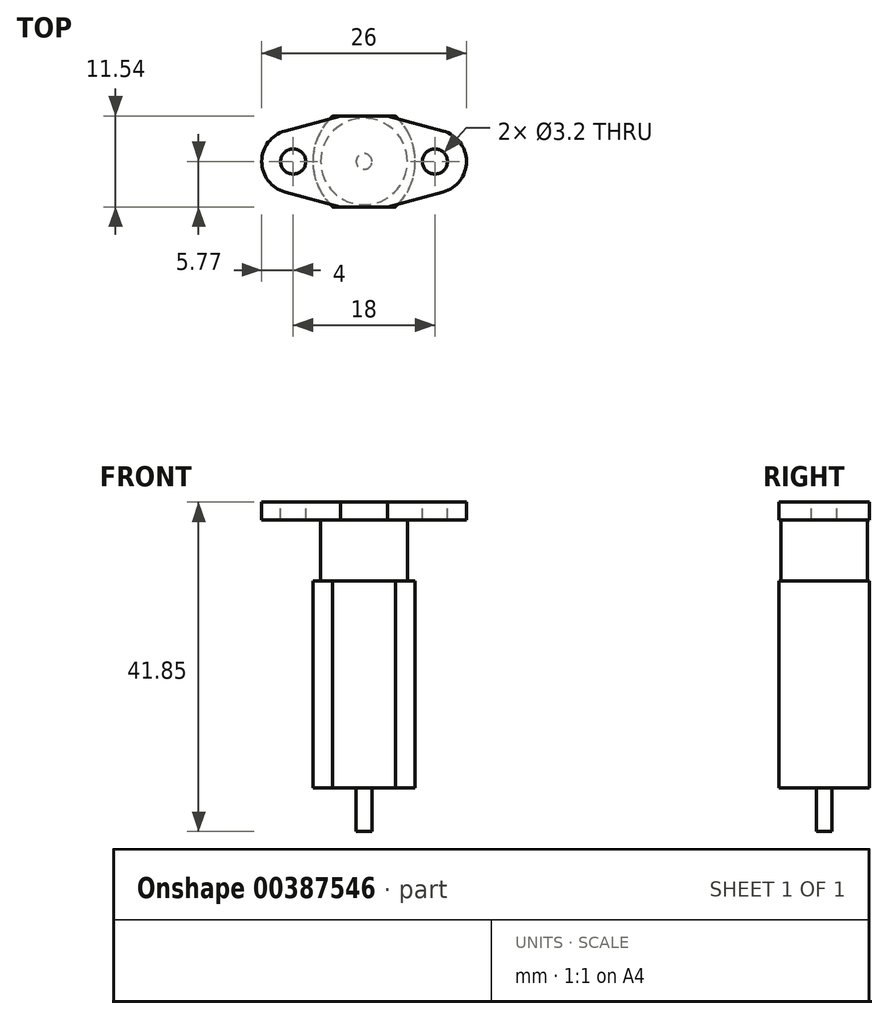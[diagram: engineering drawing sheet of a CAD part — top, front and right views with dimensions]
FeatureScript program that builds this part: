
annotation { "Feature Type Name" : "Feature", "Feature Type Description" : "" }
export const myFeature = defineFeature(function(context is Context, id is Id, definition is map)
    precondition{}
    {
        {
            var Q0;
            Q0=qCreatedBy(makeId("Top.planeOp"),FACE);
            var sketch = newSketch(context, id + "F0", { "sketchPlane" : qUnion([Q0])});
            skLineSegment(sketch, "E0", {"start": v(-3, 5.77) * mm, "end": v(3, 5.77) * mm});
            skLineSegment(sketch, "E1", {"start": v(3, 5.76) * mm, "end": v(10.04, 3.86) * mm});
            skLineSegment(sketch, "E2", {"start": v(10.04, -3.86) * mm, "end": v(3, -5.77) * mm});
            skLineSegment(sketch, "E3", {"start": v(3, -5.77) * mm, "end": v(-3, -5.77) * mm});
            skLineSegment(sketch, "E4", {"start": v(-3, -5.77) * mm, "end": v(-10.04, -3.86) * mm});
            skLineSegment(sketch, "E5", {"start": v(-10.04, 3.86) * mm, "end": v(-3, 5.77) * mm});
            skPoint(sketch, "E6.visualSharp", {"position": v(-24.33, 0) * mm});
            skArc(sketch, "E6.filletArc", {"start": v(-10.04, 3.86) * mm, "mid": v(-13, 0) * mm, "end": v(-10.04, -3.86) * mm});
            skPoint(sketch, "E7.visualSharp", {"position": v(24.33, 0) * mm});
            skArc(sketch, "E7.filletArc", {"start": v(10.04, -3.86) * mm, "mid": v(13, 0) * mm, "end": v(10.04, 3.86) * mm});
            skLineSegment(sketch, "E8", {"start": v(0, -5.77) * mm, "end": v(0, 5.77) * mm, "construction": true});
            skLineSegment(sketch, "E9", {"start": v(-9, 0) * mm, "end": v(9, 0) * mm, "construction": true});
            skCircle(sketch, "E10", {"center": v(-9, 0) * mm, "radius": 1.6 * mm});
            skCircle(sketch, "E11", {"center": v(9, 0) * mm, "radius": 1.6 * mm});
            skSolve(sketch);
        }
        {
            var Q0;
            Q0=qSketchRegion(id+"F0",true);
            extrude(context, id + "F1", {"entities" : qUnion([Q0]), "oppositeDirection" : true, "depth" : 2.3 * mm});
        }
        {
            var Q0;
            Q0=makeQuery(id+"F1.opExtrude","CAP_FACE",FACE,{"disambiguationData":[OSD([sQuery(id+"F0.wireOp",EDGE,"E0"),sQuery(id+"F0.wireOp",EDGE,"E1"),sQuery(id+"F0.wireOp",EDGE,"E2"),sQuery(id+"F0.wireOp",EDGE,"E3"),sQuery(id+"F0.wireOp",EDGE,"E4"),sQuery(id+"F0.wireOp",EDGE,"E5"),sQuery(id+"F0.wireOp",EDGE,"E6.filletArc"),sQuery(id+"F0.wireOp",EDGE,"E7.filletArc"),sQuery(id+"F0.wireOp",EDGE,"E10"),sQuery(id+"F0.wireOp",EDGE,"E11")])],"isStart":false});
            var sketch = newSketch(context, id + "F2", { "sketchPlane" : qUnion([Q0])});
            skCircle(sketch, "E12", {"center": v(0, 0) * mm, "radius": 5.5 * mm});
            skPoint(sketch, "E12.centerSnap0", {"position": v(-13, 0) * mm});
            skPoint(sketch, "E12.centerSnap1", {"position": v(0, 5.77) * mm});
            skSolve(sketch);
        }
        {
            var Q0;
            Q0=qSketchRegion(id+"F2",true);
            extrude(context, id + "F3", {"entities" : qUnion([Q0]), "operationType" : NewBodyOperationType.ADD, "depth" : 7.7 * mm});
        }
        {
            var Q0;
            Q0=makeQuery(id+"F3.opExtrude","CAP_FACE",FACE,{"disambiguationData":[OSD([sQuery(id+"F2.wireOp",EDGE,"E12")])],"isStart":false});
            var sketch = newSketch(context, id + "F4", { "sketchPlane" : qUnion([Q0])});
            skLineSegment(sketch, "E13", {"start": v(-4, 5.77) * mm, "end": v(4, 5.77) * mm});
            skLineSegment(sketch, "E14", {"start": v(4, -5.76) * mm, "end": v(-4, -5.76) * mm});
            skLineSegment(sketch, "E15", {"start": v(0, 5.77) * mm, "end": v(0, -5.77) * mm, "construction": true});
            skArc(sketch, "E16", {"start": v(-4, 5.76) * mm, "mid": v(-6.5, 0) * mm, "end": v(-4, -5.77) * mm});
            skArc(sketch, "E17", {"start": v(4, -5.76) * mm, "mid": v(6.5, 0) * mm, "end": v(4, 5.76) * mm});
            skLineSegment(sketch, "E18", {"start": v(-1.4, 0) * mm, "end": v(1.4, 0) * mm, "construction": true});
            skPoint(sketch, "E19", {"position": v(0, 0) * mm});
            skSolve(sketch);
        }
        {
            var Q0;
            Q0=qSketchRegion(id+"F4",true);
            extrude(context, id + "F5", {"entities" : qUnion([Q0]), "operationType" : NewBodyOperationType.ADD, "depth" : 26.3 * mm});
        }
        {
            var Q0;
            Q0=makeQuery(id+"F5.opExtrude","CAP_FACE",FACE,{"disambiguationData":[OSD([sQuery(id+"F4.wireOp",EDGE,"E13"),sQuery(id+"F4.wireOp",EDGE,"E14"),sQuery(id+"F4.wireOp",EDGE,"E16"),sQuery(id+"F4.wireOp",EDGE,"E17")])],"isStart":false});
            var sketch = newSketch(context, id + "F6", { "sketchPlane" : qUnion([Q0])});
            skCircle(sketch, "E20", {"center": v(0, 0) * mm, "radius": 1 * mm});
            skSolve(sketch);
        }
        {
            var Q0;
            Q0=qSketchRegion(id+"F6",true);
            extrude(context, id + "F7", {"entities" : qUnion([Q0]), "operationType" : NewBodyOperationType.ADD, "depth" : 5.55 * mm});
        }
    });
